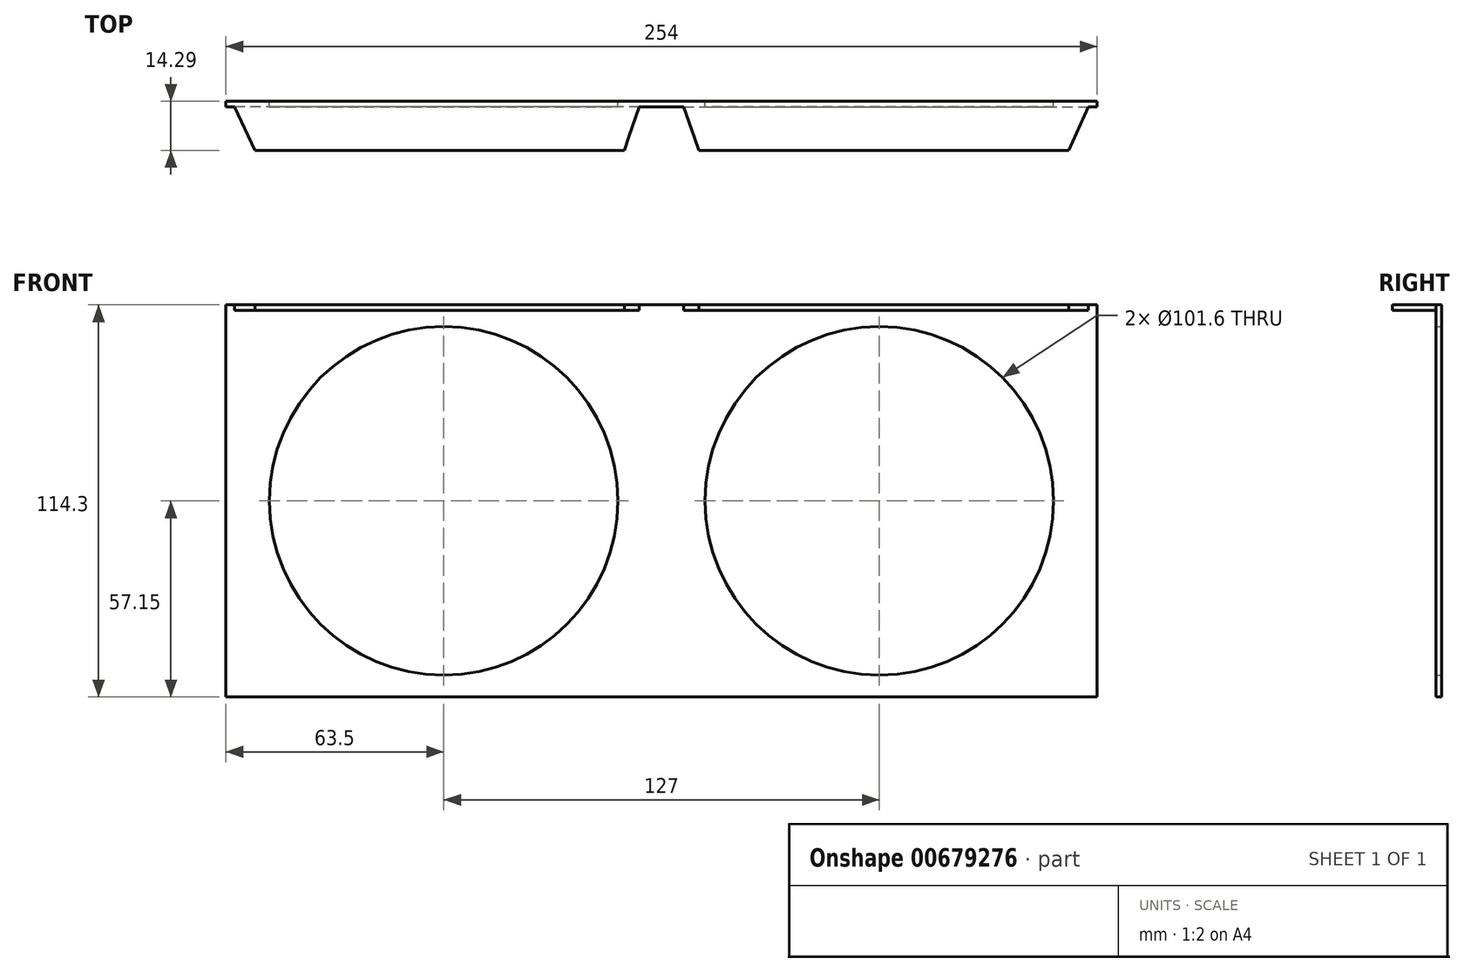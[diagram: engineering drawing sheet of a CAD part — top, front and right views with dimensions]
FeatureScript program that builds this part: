
annotation { "Feature Type Name" : "Feature", "Feature Type Description" : "" }
export const myFeature = defineFeature(function(context is Context, id is Id, definition is map)
    precondition{}
    {
        {
            var Q0;
            Q0=qCreatedBy(makeId("Front.planeOp"),FACE);
            var sketch = newSketch(context, id + "F0", { "sketchPlane" : qUnion([Q0])});
            skLineSegment(sketch, "E0.bottom", {"start": v(-127, -57.15) * mm, "end": v(127, -57.15) * mm});
            skLineSegment(sketch, "E0.top", {"start": v(-127, 57.15) * mm, "end": v(127, 57.15) * mm});
            skLineSegment(sketch, "E0.left", {"start": v(-127, -57.15) * mm, "end": v(-127, 57.15) * mm});
            skLineSegment(sketch, "E0.right", {"start": v(127, -57.15) * mm, "end": v(127, 57.15) * mm});
            skPoint(sketch, "E0.middle", {"position": v(0, 0) * mm});
            skCircle(sketch, "E1", {"center": v(63.5, 0) * mm, "radius": 50.8 * mm});
            skCircle(sketch, "E2", {"center": v(-63.5, 0) * mm, "radius": 50.8 * mm});
            skSolve(sketch);
        }
        {
            var Q0;
            Q0=qSketchRegion(id+"F0",true);
            extrude(context, id + "F1", {"entities" : qUnion([Q0]), "depth" : 1.59 * mm, "offsetDistance" : 25.4 * mm});
        }
        {
            var Q0;
            Q0=makeQuery(id+"F1.opExtrude","CAP_FACE",FACE,{"disambiguationData":[OSD([sQuery(id+"F0.wireOp",EDGE,"E0.bottom"),sQuery(id+"F0.wireOp",EDGE,"E0.top"),sQuery(id+"F0.wireOp",EDGE,"E0.left"),sQuery(id+"F0.wireOp",EDGE,"E0.right"),sQuery(id+"F0.wireOp",EDGE,"E1"),sQuery(id+"F0.wireOp",EDGE,"E2")])],"isStart":false});
            var sketch = newSketch(context, id + "F2", { "sketchPlane" : qUnion([Q0])});
            skPoint(sketch, "E3", {"position": v(-122.01, 57.15) * mm});
            skPoint(sketch, "E4", {"position": v(-9.5, 57.15) * mm});
            skPoint(sketch, "E5", {"position": v(9.59, 57.15) * mm});
            skPoint(sketch, "E6", {"position": v(121.82, 57.15) * mm});
            skLineSegment(sketch, "E7.bottom", {"start": v(-122.01, 57.15) * mm, "end": v(-9.5, 57.15) * mm});
            skLineSegment(sketch, "E7.top", {"start": v(-122.01, 55.56) * mm, "end": v(-9.5, 55.56) * mm});
            skLineSegment(sketch, "E7.right", {"start": v(-9.5, 57.15) * mm, "end": v(-9.5, 55.56) * mm});
            skLineSegment(sketch, "E8.bottom", {"start": v(9.59, 57.15) * mm, "end": v(121.82, 57.15) * mm});
            skLineSegment(sketch, "E8.top", {"start": v(9.59, 55.56) * mm, "end": v(121.82, 55.56) * mm});
            skLineSegment(sketch, "E8.left", {"start": v(9.59, 57.15) * mm, "end": v(9.59, 55.56) * mm});
            skLineSegment(sketch, "E9.bottom", {"start": v(-122.01, 55.56) * mm, "end": v(-124.52, 55.56) * mm});
            skLineSegment(sketch, "E9.top", {"start": v(-122.01, 57.15) * mm, "end": v(-124.52, 57.15) * mm});
            skLineSegment(sketch, "E9.right", {"start": v(-124.52, 55.56) * mm, "end": v(-124.52, 57.15) * mm});
            skLineSegment(sketch, "E10.bottom", {"start": v(121.82, 55.56) * mm, "end": v(124.49, 55.56) * mm});
            skLineSegment(sketch, "E10.top", {"start": v(121.82, 57.15) * mm, "end": v(124.49, 57.15) * mm});
            skLineSegment(sketch, "E10.right", {"start": v(124.49, 55.56) * mm, "end": v(124.49, 57.15) * mm});
            skSolve(sketch);
        }
        {
            var Q0;
            Q0=qSketchRegion(id+"F2",true);
            extrude(context, id + "F3", {"entities" : qUnion([Q0]), "operationType" : NewBodyOperationType.ADD, "depth" : 12.7 * mm, "offsetDistance" : 25.4 * mm});
        }
        {
            var Q0;
            Q0=makeQuery(id+"F3.boolean.opBoolean","MERGE",FACE,{"derivedFrom":[makeQuery(id+"F1.opExtrude","SWEPT_FACE",FACE,{"disambiguationData":[OSD([sQuery(id+"F0.wireOp",EDGE,"E0.top")])]}),makeQuery(id+"F3.opExtrude","SWEPT_FACE",FACE,{"disambiguationData":[OSD([sQuery(id+"F2.wireOp",EDGE,"E7.bottom"),sQuery(id+"F2.wireOp",EDGE,"E9.top")])]}),makeQuery(id+"F3.opExtrude","SWEPT_FACE",FACE,{"disambiguationData":[OSD([sQuery(id+"F2.wireOp",EDGE,"E8.bottom"),sQuery(id+"F2.wireOp",EDGE,"E10.top")])]})]});
            var sketch = newSketch(context, id + "F4", { "sketchPlane" : qUnion([Q0])});
            skLineSegment(sketch, "E11", {"start": v(-9.5, -1.59) * mm, "end": v(-9.5, -10.33) * mm});
            skLineSegment(sketch, "E12", {"start": v(-9.5, -10.33) * mm, "end": v(-6.47, -1.59) * mm});
            skLineSegment(sketch, "E13", {"start": v(-6.47, -1.59) * mm, "end": v(-9.5, -1.59) * mm});
            skLineSegment(sketch, "E14", {"start": v(9.59, -1.59) * mm, "end": v(9.59, -10.58) * mm});
            skLineSegment(sketch, "E15", {"start": v(9.59, -10.58) * mm, "end": v(6.46, -1.59) * mm});
            skLineSegment(sketch, "E16", {"start": v(6.46, -1.59) * mm, "end": v(9.59, -1.59) * mm});
            skSolve(sketch);
        }
        {
            var Q0;
            Q0 = qSketchRegion(id + "F4", true);
            extrude(context, id + "F5", {"entities" : qUnion([Q0]), "operationType" : NewBodyOperationType.ADD, "oppositeDirection" : true, "depth" : 1.59 * mm, "offsetDistance" : 25.4 * mm});
        }
        {
            var Q0;
            Q0=makeQuery(id+"F5.boolean.opBoolean","MERGE",FACE,{"derivedFrom":[makeQuery(id+"F3.boolean.opBoolean","MERGE",FACE,{"derivedFrom":[makeQuery(id+"F1.opExtrude","SWEPT_FACE",FACE,{"disambiguationData":[OSD([sQuery(id+"F0.wireOp",EDGE,"E0.top")])]}),makeQuery(id+"F3.opExtrude","SWEPT_FACE",FACE,{"disambiguationData":[OSD([sQuery(id+"F2.wireOp",EDGE,"E7.bottom"),sQuery(id+"F2.wireOp",EDGE,"E9.top")])]}),makeQuery(id+"F3.opExtrude","SWEPT_FACE",FACE,{"disambiguationData":[OSD([sQuery(id+"F2.wireOp",EDGE,"E8.bottom"),sQuery(id+"F2.wireOp",EDGE,"E10.top")])]})]}),makeQuery(id+"F5.opExtrude","CAP_FACE",FACE,{"disambiguationData":[OSD([sQuery(id+"F4.wireOp",EDGE,"E11"),sQuery(id+"F4.wireOp",EDGE,"E12"),sQuery(id+"F4.wireOp",EDGE,"E13")])],"isStart":true}),makeQuery(id+"F5.opExtrude","CAP_FACE",FACE,{"disambiguationData":[OSD([sQuery(id+"F4.wireOp",EDGE,"E14"),sQuery(id+"F4.wireOp",EDGE,"E15"),sQuery(id+"F4.wireOp",EDGE,"E16")])],"isStart":true})]});
            var sketch = newSketch(context, id + "F6", { "sketchPlane" : qUnion([Q0])});
            skLineSegment(sketch, "E17", {"start": v(-9.5, -14.29) * mm, "end": v(-10.9, -14.29) * mm});
            skLineSegment(sketch, "E18", {"start": v(-10.9, -14.29) * mm, "end": v(-9.5, -10.33) * mm});
            skLineSegment(sketch, "E19", {"start": v(-9.5, -10.33) * mm, "end": v(-9.5, -14.29) * mm});
            skLineSegment(sketch, "E20", {"start": v(9.59, -14.29) * mm, "end": v(10.89, -14.29) * mm});
            skLineSegment(sketch, "E21", {"start": v(10.89, -14.29) * mm, "end": v(9.59, -10.58) * mm});
            skLineSegment(sketch, "E22", {"start": v(9.59, -10.58) * mm, "end": v(9.59, -14.29) * mm});
            skSolve(sketch);
        }
        {
            var Q0;
            Q0 = qSketchRegion(id + "F6", true);
            extrude(context, id + "F7", {"entities" : qUnion([Q0]), "operationType" : NewBodyOperationType.REMOVE, "oppositeDirection" : true, "depth" : 25.4 * mm, "offsetDistance" : 25.4 * mm});
        }
        {
            var Q0;
            Q0=makeQuery(id+"F5.boolean.opBoolean","MERGE",FACE,{"derivedFrom":[makeQuery(id+"F3.boolean.opBoolean","MERGE",FACE,{"derivedFrom":[makeQuery(id+"F1.opExtrude","SWEPT_FACE",FACE,{"disambiguationData":[OSD([sQuery(id+"F0.wireOp",EDGE,"E0.top")])]}),makeQuery(id+"F3.opExtrude","SWEPT_FACE",FACE,{"disambiguationData":[OSD([sQuery(id+"F2.wireOp",EDGE,"E7.bottom"),sQuery(id+"F2.wireOp",EDGE,"E9.top")])]}),makeQuery(id+"F3.opExtrude","SWEPT_FACE",FACE,{"disambiguationData":[OSD([sQuery(id+"F2.wireOp",EDGE,"E8.bottom"),sQuery(id+"F2.wireOp",EDGE,"E10.top")])]})]}),makeQuery(id+"F5.opExtrude","CAP_FACE",FACE,{"disambiguationData":[OSD([sQuery(id+"F4.wireOp",EDGE,"E11"),sQuery(id+"F4.wireOp",EDGE,"E12"),sQuery(id+"F4.wireOp",EDGE,"E13")])],"isStart":true}),makeQuery(id+"F5.opExtrude","CAP_FACE",FACE,{"disambiguationData":[OSD([sQuery(id+"F4.wireOp",EDGE,"E14"),sQuery(id+"F4.wireOp",EDGE,"E15"),sQuery(id+"F4.wireOp",EDGE,"E16")])],"isStart":true})]});
            var sketch = newSketch(context, id + "F8", { "sketchPlane" : qUnion([Q0])});
            skLineSegment(sketch, "E23", {"start": v(-124.52, -1.59) * mm, "end": v(-118.56, -14.29) * mm});
            skLineSegment(sketch, "E24", {"start": v(-118.56, -14.29) * mm, "end": v(-124.52, -14.29) * mm});
            skLineSegment(sketch, "E25", {"start": v(-124.52, -14.29) * mm, "end": v(-124.52, -1.59) * mm});
            skLineSegment(sketch, "E26", {"start": v(124.49, -1.59) * mm, "end": v(118.7, -14.29) * mm});
            skLineSegment(sketch, "E27", {"start": v(118.7, -14.29) * mm, "end": v(124.49, -14.29) * mm});
            skLineSegment(sketch, "E28", {"start": v(124.49, -14.29) * mm, "end": v(124.49, -1.59) * mm});
            skSolve(sketch);
        }
        {
            var Q0;
            Q0 = qSketchRegion(id + "F8", true);
            extrude(context, id + "F9", {"entities" : qUnion([Q0]), "operationType" : NewBodyOperationType.REMOVE, "oppositeDirection" : true, "depth" : 25.4 * mm, "offsetDistance" : 25.4 * mm});
        }
    });
